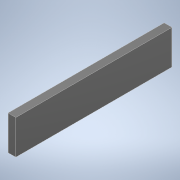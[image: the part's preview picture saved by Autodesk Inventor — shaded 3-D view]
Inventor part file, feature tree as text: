
AUTODESK INVENTOR PART (.ipt)
format: ipt  version: 2021 (Build 250183000, 183)  size: 93,184 bytes
history: native  units: mm
features: extrude x1, sketch x1
ambient origin geometry x8: Origin, YZ Plane, XZ Plane, XY Plane, X Axis, Y Axis, Z Axis, Center Point
bodies: Solid1 (feature_tree)
feature tree (2):
  extrude  "Extrusion1"  Depth=100.0mm
  sketch  "Sketch1"  dims[d0=22.0mm d1=100.0mm d2=5.0mm d3=0.0mm]
